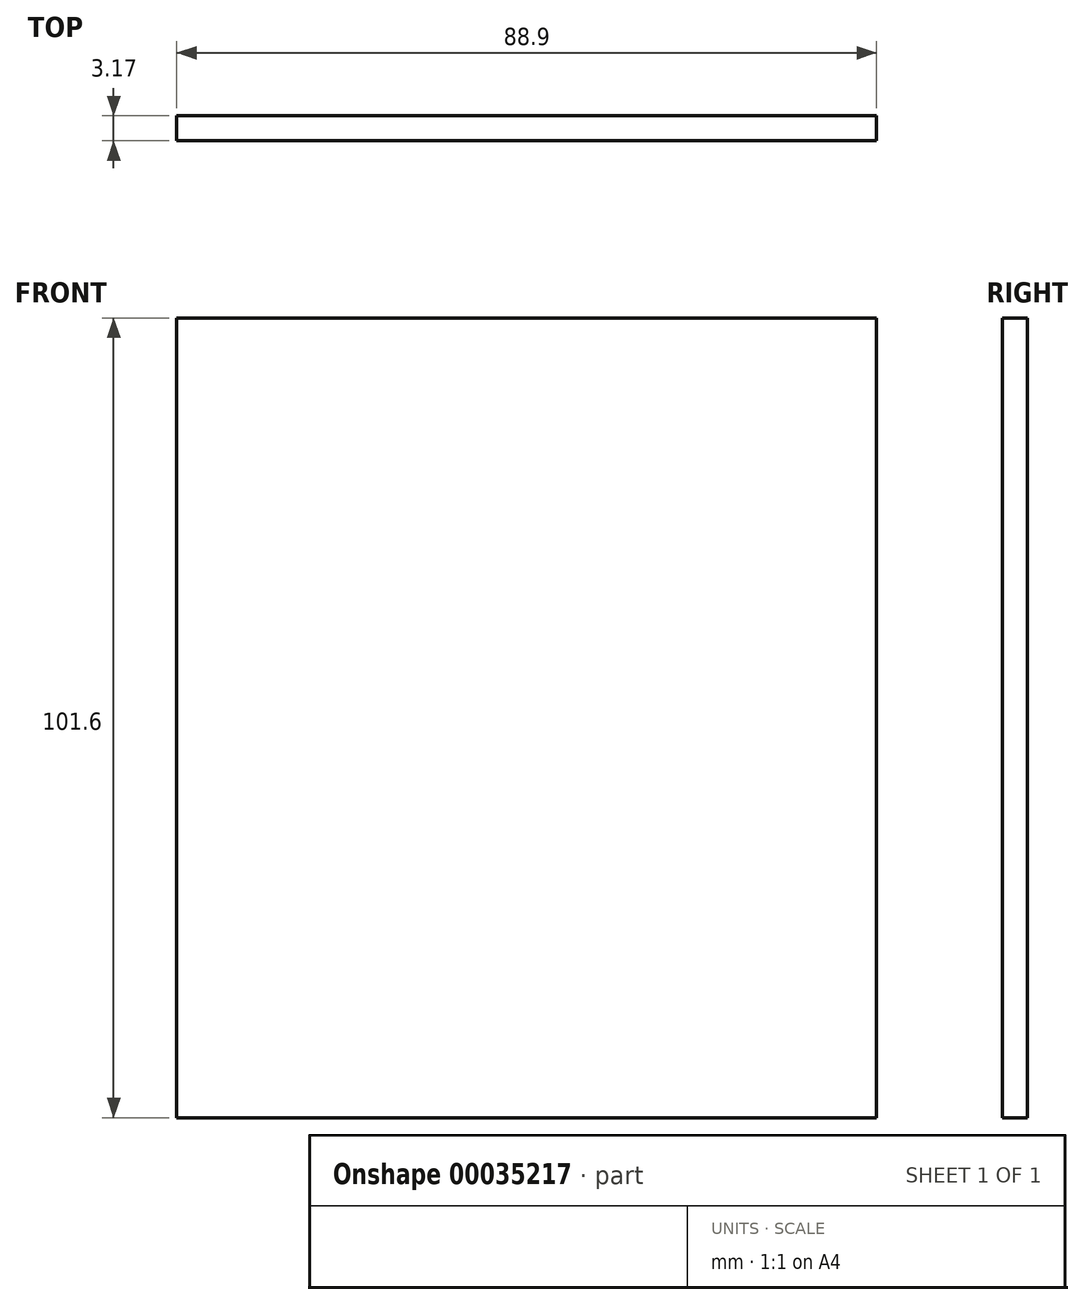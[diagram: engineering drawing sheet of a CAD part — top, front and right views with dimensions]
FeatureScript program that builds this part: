
annotation { "Feature Type Name" : "Feature", "Feature Type Description" : "" }
export const myFeature = defineFeature(function(context is Context, id is Id, definition is map)
    precondition{}
    {
        {
            var Q0;
            Q0=qCreatedBy(makeId("Front.planeOp"),FACE);
            var sketch = newSketch(context, id + "F0", { "sketchPlane" : qUnion([Q0])});
            skLineSegment(sketch, "E0.bottom", {"start": v(41.19, 49.03) * mm, "end": v(-47.71, 49.03) * mm});
            skLineSegment(sketch, "E0.top", {"start": v(41.19, -52.57) * mm, "end": v(-47.71, -52.57) * mm});
            skLineSegment(sketch, "E0.left", {"start": v(41.19, 49.03) * mm, "end": v(41.19, -52.57) * mm});
            skLineSegment(sketch, "E0.right", {"start": v(-47.71, 49.03) * mm, "end": v(-47.71, -52.57) * mm});
            skSolve(sketch);
        }
        {
            var Q0;
            Q0=makeQuery(id+"F0.imprint","IMPRINT",FACE,{"disambiguationData":[TD([[makeQuery(id+"F0.imprint","IMPRINT",EDGE,{"derivedFrom":sQuery(id+"F0.wireOp",EDGE,"E0.bottom")}),1.0]])]});
            extrude(context, id + "F1", {"entities" : qUnion([Q0]), "depth" : 3.17 * mm});
        }
    });
